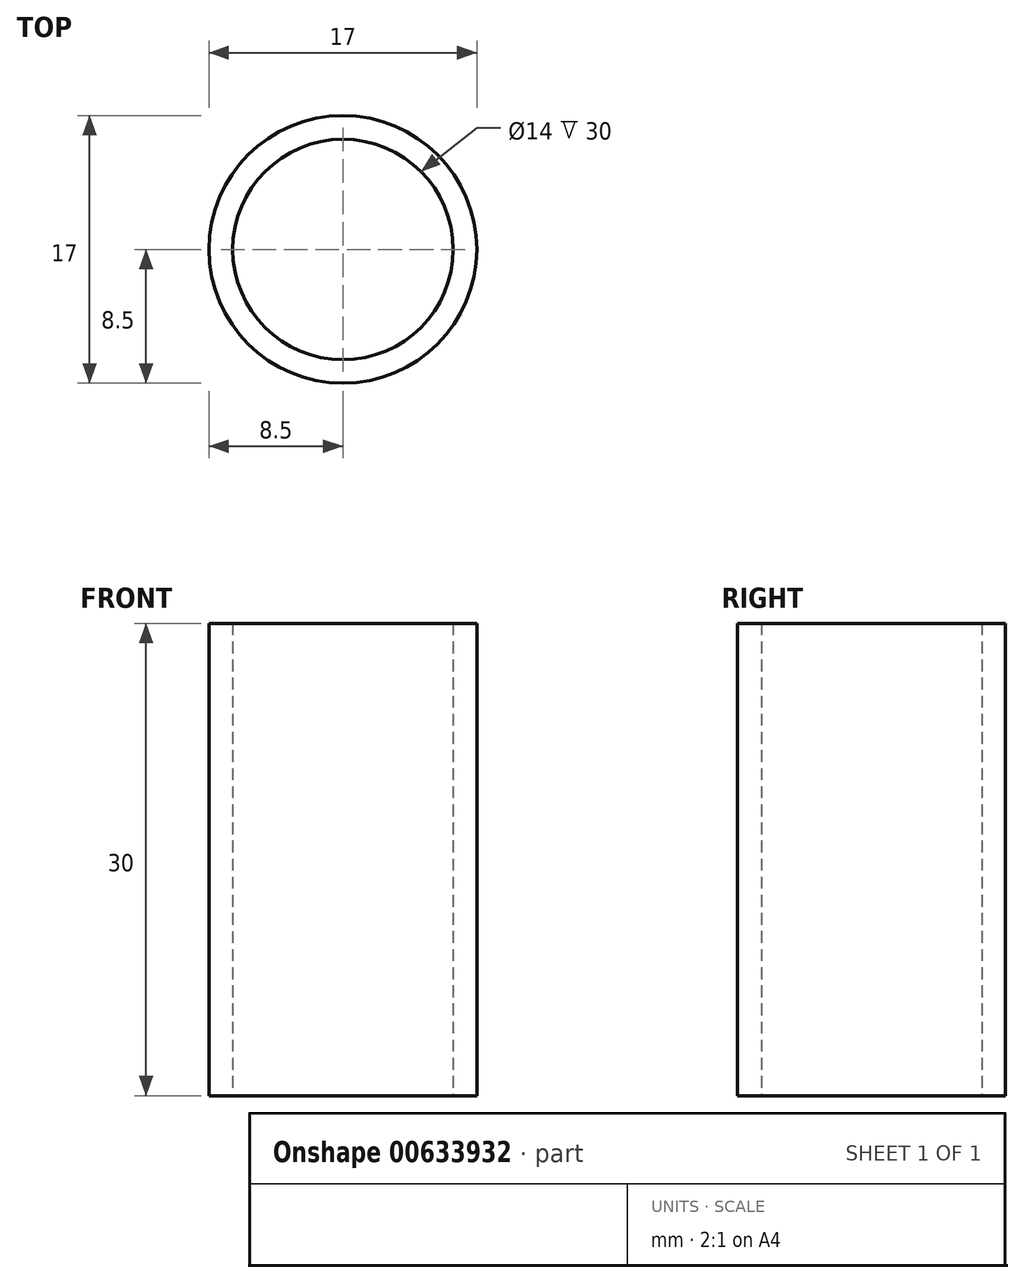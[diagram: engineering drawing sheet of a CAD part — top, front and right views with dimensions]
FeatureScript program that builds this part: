
annotation { "Feature Type Name" : "Feature", "Feature Type Description" : "" }
export const myFeature = defineFeature(function(context is Context, id is Id, definition is map)
    precondition{}
    {
        {
            var Q0;
            Q0=qCreatedBy(makeId("Top.planeOp"),FACE);
            var sketch = newSketch(context, id + "F0", { "sketchPlane" : qUnion([Q0])});
            skCircle(sketch, "E0", {"center": v(0, 0) * mm, "radius": 7 * mm});
            skCircle(sketch, "E1", {"center": v(0, 0) * mm, "radius": 8.5 * mm});
            skSolve(sketch);
        }
        {
            var Q0;
            Q0=qSketchRegion(id+"F0",true);
            extrude(context, id + "F1", {"entities" : qUnion([Q0]), "depth" : 30 * mm, "offsetDistance" : 25 * mm});
        }
        {
            var Q0;
            Q0=makeQuery(id+"F1.opExtrude","CAP_FACE",FACE,{"disambiguationData":[OSD([sQuery(id+"F0.wireOp",EDGE,"E0"),sQuery(id+"F0.wireOp",EDGE,"E1")])],"isStart":true});
            var sketch = newSketch(context, id + "F2", { "sketchPlane" : qUnion([Q0])});
            skCircle(sketch, "E2", {"center": v(0, 0) * mm, "radius": 20 * mm});
            skSolve(sketch);
        }
        {
            var Q0;
            Q0=qSketchRegion(id+"F2",true);
            extrude(context, id + "F3", {"entities" : qUnion([Q0]), "operationType" : NewBodyOperationType.ADD, "depth" : 34 * mm, "offsetDistance" : 25 * mm});
        }
        {
            var Q0;
            Q0=makeQuery(id+"F3.opExtrude","CAP_FACE",FACE,{"disambiguationData":[OSD([sQuery(id+"F2.wireOp",EDGE,"E2")])],"isStart":false});
            var sketch = newSketch(context, id + "F4", { "sketchPlane" : qUnion([Q0])});
            skLineSegment(sketch, "E3", {"start": v(0, 0) * mm, "end": v(-20, 0) * mm, "construction": true});
            skLineSegment(sketch, "E4", {"start": v(0, 0) * mm, "end": v(20, 0) * mm, "construction": true});
            skLineSegment(sketch, "E5", {"start": v(0, 0) * mm, "end": v(0, 20) * mm, "construction": true});
            skLineSegment(sketch, "E6", {"start": v(0, 0) * mm, "end": v(0, -20) * mm, "construction": true});
            skSolve(sketch);
        }
        {
            var Q0;
            Q0=sQuery(id+"F4.wireOp",VERTEX,"E6.start");
            var Q1;
            Q1=makeQuery(id+"F1.opExtrude","SWEPT_BODY",BODY,{"disambiguationData":[OSD([sQuery(id+"F0.wireOp",EDGE,"E0"),sQuery(id+"F0.wireOp",EDGE,"E1")])]});
            hole(context, id + "F5", {"style" : HoleStyle.C_SINK, "endStyle" : HoleEndStyle.THROUGH, "holeDiameter" : 14 * mm, "cSinkDiameter" : 40 * mm, "cSinkAngle" : 47 * degree, "majorDiameter" : 5 * mm, "isTappedThrough" : true, "tappedDepth" : 12 * mm, "tapClearance" : 3, "locations" : qUnion([Q0]), "scope" : qUnion([Q1])});
        }
        {
            var Q0;
            Q0=makeQuery(id+"F3.opExtrude","CAP_EDGE",EDGE,{"disambiguationData":[OSD([sQuery(id+"F2.wireOp",EDGE,"E2")])],"isStart":true});
            chamfer(context, id + "F6", {"entities" : qUnion([Q0]), "chamferType" : ChamferType.OFFSET_ANGLE, "width" : 30 * mm, "oppositeDirection" : false, "angle" : 20 * degree, "tangentPropagation" : true});
        }
        {
            var Q0;
            {var subQ0=sQuery(id+"F2.wireOp",EDGE,"E2");Q0=makeQuery(id+"F6.opChamfer","BLEND_EDGE",EDGE,{"blendedFrom":[makeQuery(id+"F3.opExtrude","CAP_EDGE",EDGE,{"disambiguationData":[OSD([subQ0])],"isStart":true}),makeQuery(id+"F3.boolean.opBoolean","SPLIT",FACE,{"disambiguationData":[TD([makeQuery(id+"F1.opExtrude","SWEPT_FACE",FACE,{"disambiguationData":[OSD([sQuery(id+"F0.wireOp",EDGE,"E1")])]})])],"derivedFrom":makeQuery(id+"F3.opExtrude","CAP_FACE",FACE,{"disambiguationData":[OSD([subQ0])],"isStart":true})})],"blendedInto":[makeQuery(id+"F3.boolean.opBoolean","SPLIT",FACE,{"disambiguationData":[TD([makeQuery(id+"F1.opExtrude","SWEPT_FACE",FACE,{"disambiguationData":[OSD([sQuery(id+"F0.wireOp",EDGE,"E1")])]})])],"derivedFrom":makeQuery(id+"F3.opExtrude","CAP_FACE",FACE,{"disambiguationData":[OSD([subQ0])],"isStart":true})})]});}
            chamfer(context, id + "F7", {"entities" : qUnion([Q0]), "chamferType" : ChamferType.OFFSET_ANGLE, "width" : .5 * mm, "oppositeDirection" : false, "angle" : 55 * degree, "tangentPropagation" : true});
        }
        {
            var Q0;
            Q0=qCreatedBy(makeId("Front.planeOp"),FACE);
            var sketch = newSketch(context, id + "F8", { "sketchPlane" : qUnion([Q0])});
            skLineSegment(sketch, "E7.bottom", {"start": v(-34.2, -44.85) * mm, "end": v(53.73, -44.85) * mm});
            skLineSegment(sketch, "E7.top", {"start": v(-34.2, 0) * mm, "end": v(53.73, 0) * mm});
            skLineSegment(sketch, "E7.left", {"start": v(-34.2, -44.85) * mm, "end": v(-34.2, 0) * mm});
            skLineSegment(sketch, "E7.right", {"start": v(53.73, -44.85) * mm, "end": v(53.73, 0) * mm});
            skSolve(sketch);
        }
        {
            var Q0;
            Q0 = qSketchRegion(id + "F8", true);
            extrude(context, id + "F9", {"entities" : qUnion([Q0]), "operationType" : NewBodyOperationType.REMOVE, "endBound" : BoundingType.THROUGH_ALL, "oppositeDirection" : true, "depth" : 25 * mm, "offsetDistance" : 25 * mm});
        }
        {
            var Q0;
            Q0 = qSketchRegion(id + "F8", true);
            extrude(context, id + "F10", {"entities" : qUnion([Q0]), "operationType" : NewBodyOperationType.REMOVE, "endBound" : BoundingType.THROUGH_ALL, "depth" : 25 * mm, "offsetDistance" : 25 * mm});
        }
    });
